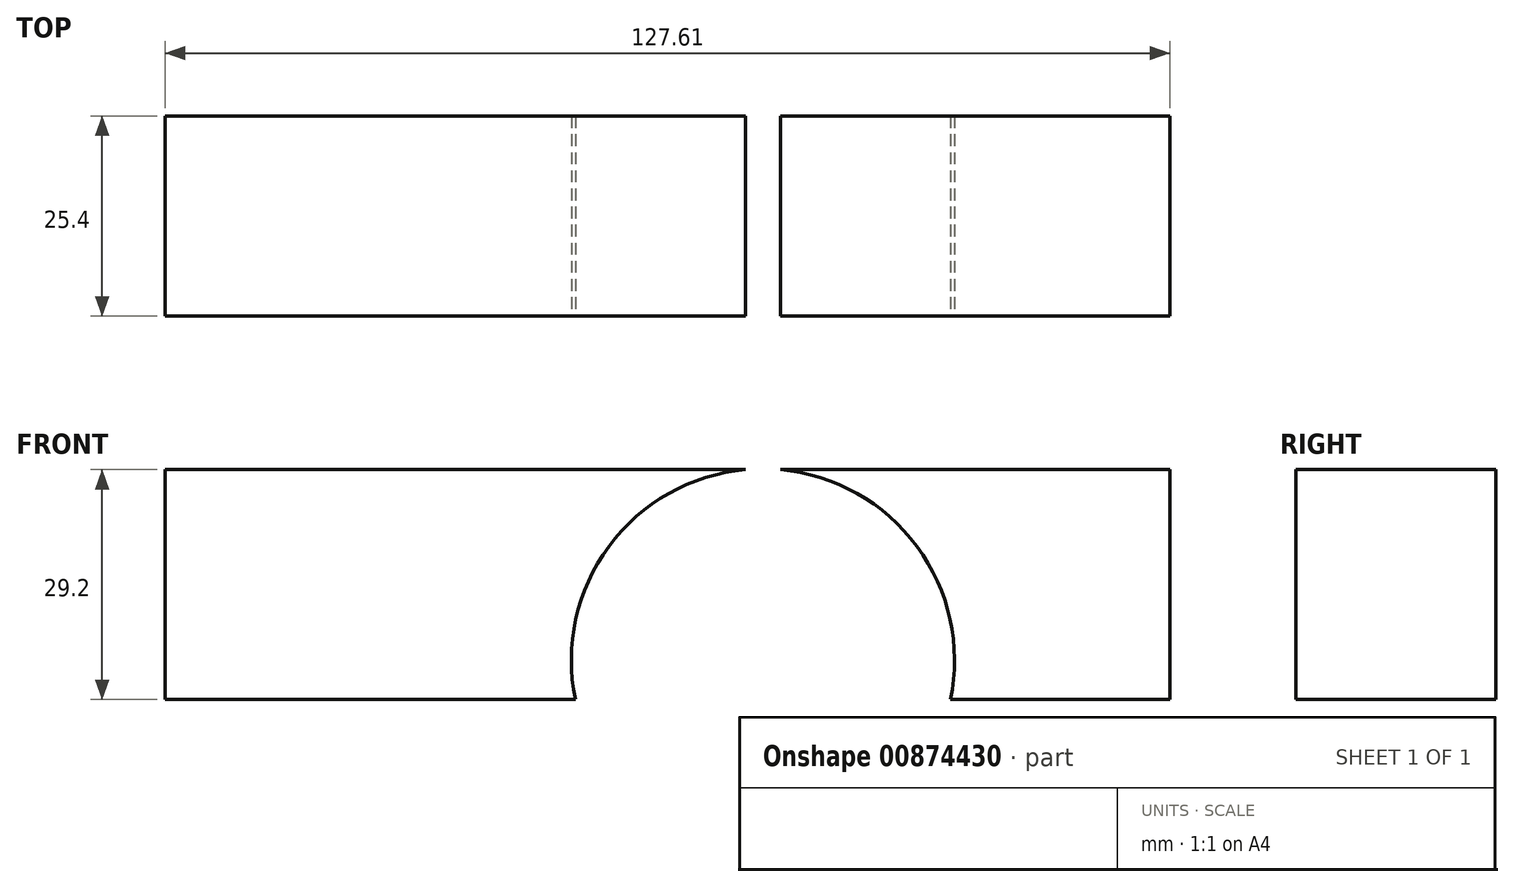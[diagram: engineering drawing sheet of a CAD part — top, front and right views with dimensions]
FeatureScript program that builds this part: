
annotation { "Feature Type Name" : "Feature", "Feature Type Description" : "" }
export const myFeature = defineFeature(function(context is Context, id is Id, definition is map)
    precondition{}
    {
        {
            var Q0;
            Q0=qCreatedBy(makeId("Front.planeOp"),FACE);
            var sketch = newSketch(context, id + "F0", { "sketchPlane" : qUnion([Q0])});
            skLineSegment(sketch, "E0.bottom", {"start": v(-60.6, 38.4) * mm, "end": v(67.02, 38.4) * mm});
            skLineSegment(sketch, "E0.top", {"start": v(-60.6, 9.2) * mm, "end": v(67.02, 9.2) * mm});
            skLineSegment(sketch, "E0.left", {"start": v(-60.6, 38.4) * mm, "end": v(-60.6, 9.2) * mm});
            skLineSegment(sketch, "E0.right", {"start": v(67.02, 38.4) * mm, "end": v(67.02, 9.2) * mm});
            skLineSegment(sketch, "E1.bottom", {"start": v(-60.6, 9.2) * mm, "end": v(-70.81, 9.2) * mm});
            skLineSegment(sketch, "E1.top", {"start": v(-60.6, 4.53) * mm, "end": v(-70.81, 4.53) * mm});
            skLineSegment(sketch, "E1.left", {"start": v(-60.6, 9.2) * mm, "end": v(-60.6, 4.53) * mm});
            skLineSegment(sketch, "E1.right", {"start": v(-70.81, 9.2) * mm, "end": v(-70.81, 4.53) * mm});
            skPoint(sketch, "E2.firstSnap0", {"position": v(-65.7, 4.53) * mm});
            skLineSegment(sketch, "E2.bottom", {"start": v(-65.7, 7.15) * mm, "end": v(-24.1, 7.15) * mm});
            skLineSegment(sketch, "E2.top", {"start": v(-65.7, -29.93) * mm, "end": v(-24.1, -29.93) * mm});
            skLineSegment(sketch, "E2.left", {"start": v(-65.7, 7.15) * mm, "end": v(-65.7, -29.93) * mm});
            skLineSegment(sketch, "E2.right", {"start": v(-24.1, 7.15) * mm, "end": v(-24.1, -29.93) * mm});
            skLineSegment(sketch, "E3.bottom", {"start": v(20, -29.93) * mm, "end": v(40.44, -29.93) * mm});
            skLineSegment(sketch, "E3.top", {"start": v(20, -45.12) * mm, "end": v(40.44, -45.12) * mm});
            skLineSegment(sketch, "E3.left", {"start": v(20, -29.93) * mm, "end": v(20, -45.12) * mm});
            skLineSegment(sketch, "E3.right", {"start": v(40.44, -29.93) * mm, "end": v(40.44, -45.12) * mm});
            skSolve(sketch);
        }
        {
            var Q0;
            Q0=makeQuery(id+"F0.imprint","IMPRINT",FACE,{"disambiguationData":[TD([[makeQuery(id+"F0.imprint","IMPRINT",EDGE,{"derivedFrom":sQuery(id+"F0.wireOp",EDGE,"E0.bottom")}),-1.0]])]});
            extrude(context, id + "F1", {"entities" : qUnion([Q0]), "depth" : 25.4 * mm, "offsetDistance" : 25.4 * mm});
        }
        {
            var Q0;
            Q0=makeQuery(id+"F1.opExtrude","CAP_FACE",FACE,{"disambiguationData":[OSD([sQuery(id+"F0.wireOp",EDGE,"E0.bottom"),sQuery(id+"F0.wireOp",EDGE,"E0.top"),sQuery(id+"F0.wireOp",EDGE,"E0.left"),sQuery(id+"F0.wireOp",EDGE,"E0.right")])],"isStart":false});
            var sketch = newSketch(context, id + "F2", { "sketchPlane" : qUnion([Q0])});
            skCircle(sketch, "E4", {"center": v(15.33, 14.16) * mm, "radius": 24.34 * mm});
            skSolve(sketch);
        }
        {
            var Q0;
            Q0 = qSketchRegion(id + "F2", true);
            extrude(context, id + "F3", {"entities" : qUnion([Q0]), "operationType" : NewBodyOperationType.REMOVE, "oppositeDirection" : true, "depth" : 50.8 * mm, "offsetDistance" : 25.4 * mm});
        }
    });
